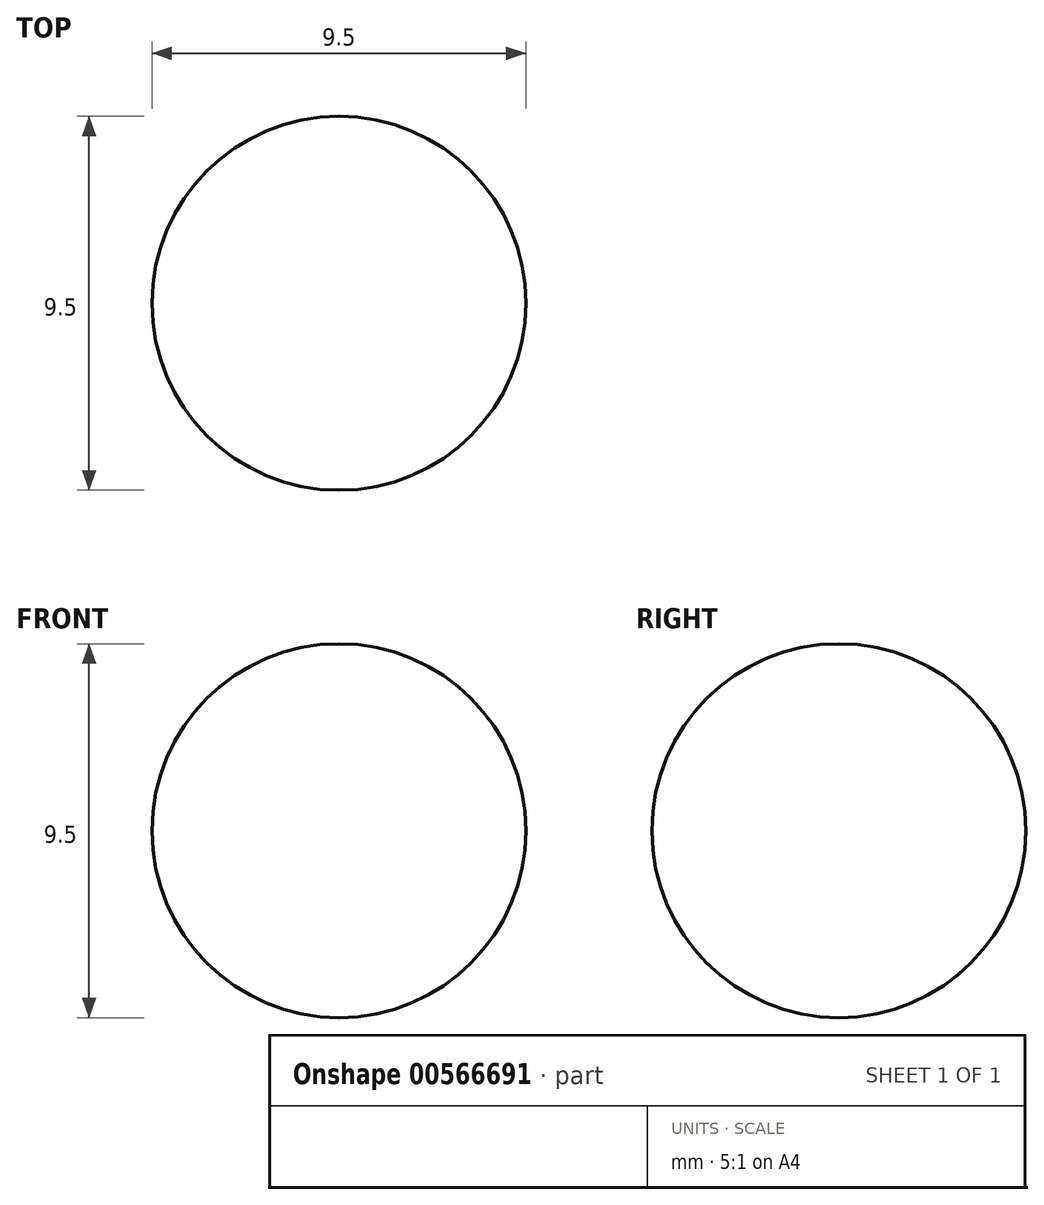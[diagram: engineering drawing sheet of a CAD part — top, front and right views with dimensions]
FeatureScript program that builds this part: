
annotation { "Feature Type Name" : "Feature", "Feature Type Description" : "" }
export const myFeature = defineFeature(function(context is Context, id is Id, definition is map)
    precondition{}
    {
        {
            var Q0;
            Q0=qCreatedBy(makeId("Front.planeOp"),FACE);
            var sketch = newSketch(context, id + "F0", { "sketchPlane" : qUnion([Q0])});
            skArc(sketch, "E0", {"start": v(0, -4.75) * mm, "mid": v(4.75, 0) * mm, "end": v(0, 4.75) * mm});
            skLineSegment(sketch, "E1", {"start": v(0, 4.75) * mm, "end": v(0, -4.75) * mm});
            skSolve(sketch);
        }
        {
            var Q0;
            Q0=qSketchRegion(id+"F0",true);
            var Q1;
            Q1=sQuery(id+"F0.wireOp",EDGE,"E1");
            revolve(context, id + "F1", {"entities" : qUnion([Q0]), "axis" : qUnion([Q1]), "revolveType" : RevolveType.FULL});
        }
    });
